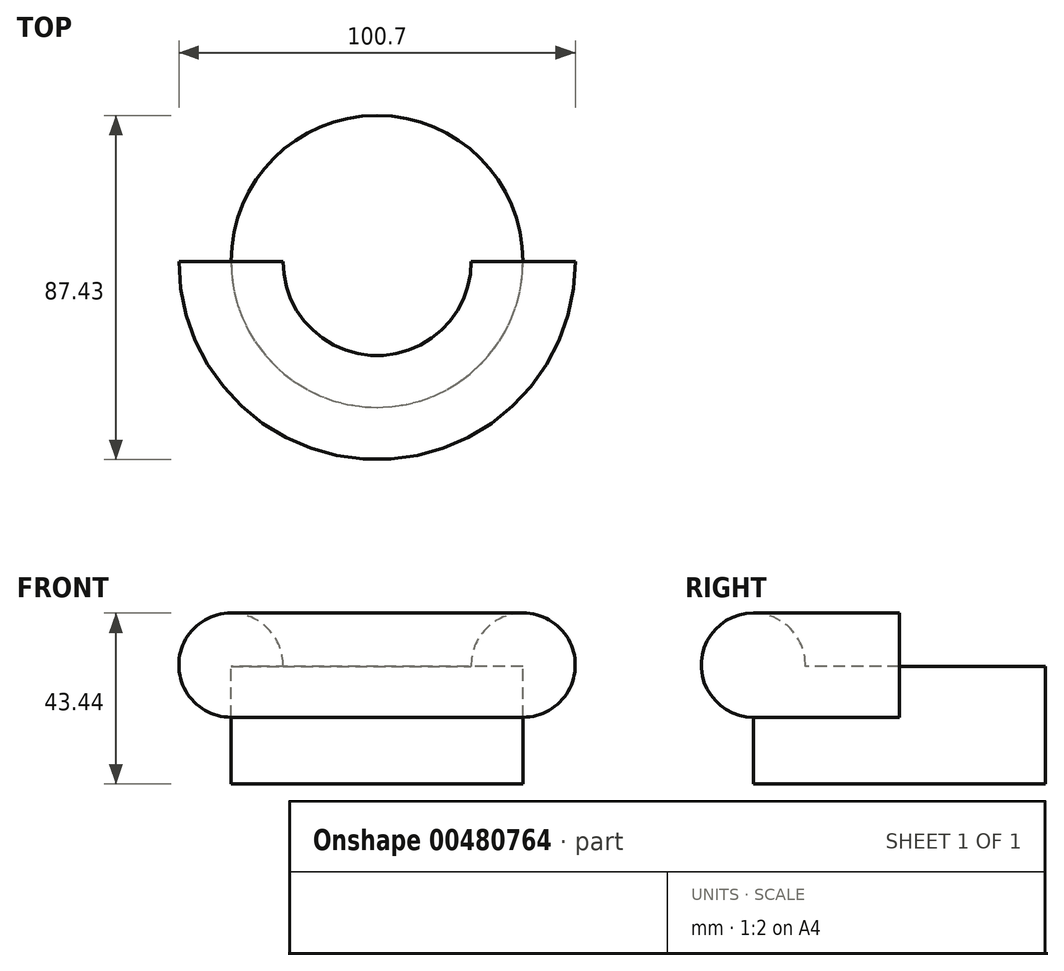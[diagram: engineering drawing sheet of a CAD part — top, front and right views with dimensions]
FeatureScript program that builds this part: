
annotation { "Feature Type Name" : "Feature", "Feature Type Description" : "" }
export const myFeature = defineFeature(function(context is Context, id is Id, definition is map)
    precondition{}
    {
        {
            var Q0;
            Q0=qCreatedBy(makeId("Right.planeOp"),FACE);
            var sketch = newSketch(context, id + "F0", { "sketchPlane" : qUnion([Q0])});
            skLineSegment(sketch, "E0", {"start": v(0, 0) * mm, "end": v(-37.08, 0) * mm});
            skLineSegment(sketch, "E1", {"start": v(-37.08, 0) * mm, "end": v(-37.08, 29.89) * mm});
            skLineSegment(sketch, "E2", {"start": v(-37.08, 29.89) * mm, "end": v(0, 29.89) * mm});
            skLineSegment(sketch, "E3", {"start": v(0, 29.89) * mm, "end": v(0, 0) * mm});
            skSolve(sketch);
        }
        {
            var Q0;
            Q0=qCreatedBy(makeId("Front.planeOp"),FACE);
            var sketch = newSketch(context, id + "F1", { "sketchPlane" : qUnion([Q0])});
            skLineSegment(sketch, "E4", {"start": v(0, 0) * mm, "end": v(0, 72.2) * mm});
            skLineSegment(sketch, "E5", {"start": v(0, 72.2) * mm, "end": v(0, -47.09) * mm, "construction": true});
            skSolve(sketch);
        }
        {
            var Q0;
            Q0 = qSketchRegion(id + "F0", true);
            var Q1;
            Q1=sQuery(id+"F1.wireOp",EDGE,"E5");
            revolve(context, id + "F2", {"entities" : qUnion([Q0]), "axis" : qUnion([Q1]), "revolveType" : RevolveType.FULL});
        }
        {
            var Q0;
            Q0=qCreatedBy(makeId("Front.planeOp"),FACE);
            var sketch = newSketch(context, id + "F3", { "sketchPlane" : qUnion([Q0])});
            skCircle(sketch, "E6", {"center": v(37.13, 30.22) * mm, "radius": 13.22 * mm});
            skSolve(sketch);
        }
        {
            var Q0;
            Q0 = qSketchRegion(id + "F3", true);
            var Q1;
            Q1=sQuery(id+"F1.wireOp",EDGE,"E5");
            revolve(context, id + "F4", {"operationType" : NewBodyOperationType.ADD, "entities" : qUnion([Q0]), "axis" : qUnion([Q1]), "revolveType" : RevolveType.ONE_DIRECTION, "angle" : 180 * degree});
        }
    });
